# Revit family: GDP2X
name_source: partatom
category: Electrical Fixtures
units: mm (PartAtom-declared; Revit-internal decimal feet)

## family parameters
Always vertical = Yes
Cut with Voids When Loaded = No
Maintain Annotation Orientation = No
Part Type = Normal
Room Calculation Point = No
Round Connector Dimension = Use Diameter
Shared = No
Work Plane-Based = No

## types (1)
- GDP2X
    Audible Alarm Buzzer dB = 65 dB (300mm distance in quiet conditions)
    Current Consumption = 12W max (50mA) @ 120VAC
    Default Elevation = 0.00"
    Description = The UL 61010 listed Merlin 1000S Laboratory Utility Controller has been designed specifically for use in School and
University Laboratories. This controller is to be used to carry out a gas proving test on the pipe work in order to highlight if
there is a gas appliance open or a gas leak in the laboratory. The Merlin 1000S is designed to give the teacher full control
over the incoming gas supply with the lockable key-switch operation. In built connectivity allows for connection to existing fire
alarm and building management systems and with its easy to use system status panel and labeled PCB the Merlin 1000S is
easy to install and to operate.
The Merlin 1000S can work in conjunction with carbon dioxide, natural gas, carbon monoxide and LPG sensors. The Merlin
1000S also has a built in “timeout” facility which will automatically shut off the gas solenoid valve at the end of a specific time
period, this time period can be adjusted to 2, 4, 8 hours or can be overridden if required.
    Flame Rating = UL 94
    Gas Valve Output = 3.15A
    Housing Material = Polylac PA-765 Flame Retardant
    Internal Fuse = 3.15A
    Mains Electrical Power Input = 110-120VAC
    Manufacturer = American Gas Safety LLC
    Model = Merlin 1000S
    O/All Dimensions (H x W x D) inch = 7.08 x 10 x 3.03"
    Operating Temperature = 32 - 104°F 0-95%RH Non-Condensing
    PANNEL BODY = PANNEL BODY
    Pressure Sensor Operating Pressure = 0-1.45psi
    Tel = (727) 608-4375
    UL Approval Reference = UL 61010-1 E464760
    URL = https://americangassafety.com
    Utility Output = 110-120VAC
    Visual Indication = LED

## geometry (parser evidence)
native form markers: Sweep x45
no freeform markers — native parametric forms only
